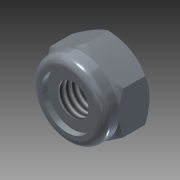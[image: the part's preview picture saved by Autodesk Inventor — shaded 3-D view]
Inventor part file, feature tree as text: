
AUTODESK INVENTOR PART (.ipt)
format: ipt  version: 2016 SP1 (Build 200210100, 210)  size: 150,016 bytes
history: native  units: in
note: dims shown in document units (in); Inventor stores cm internally (conversion verified against a paired STEP export)
features: thread x1, fillet x1
ambient origin geometry x8: Origin, YZ Plane, XZ Plane, XY Plane, X Axis, Y Axis, Z Axis, Center Point
bodies: Solid1 (feature_tree)
feature tree (2):
  thread  "Thread1"  [1 undecoded]
  fillet  "Fillet1"  [1 undecoded]
note: 2 required parameter values undecoded (feature->parameter linkage not recoverable at this tier; creation-order binding heuristic only, values carry confidence <= 0.55)
